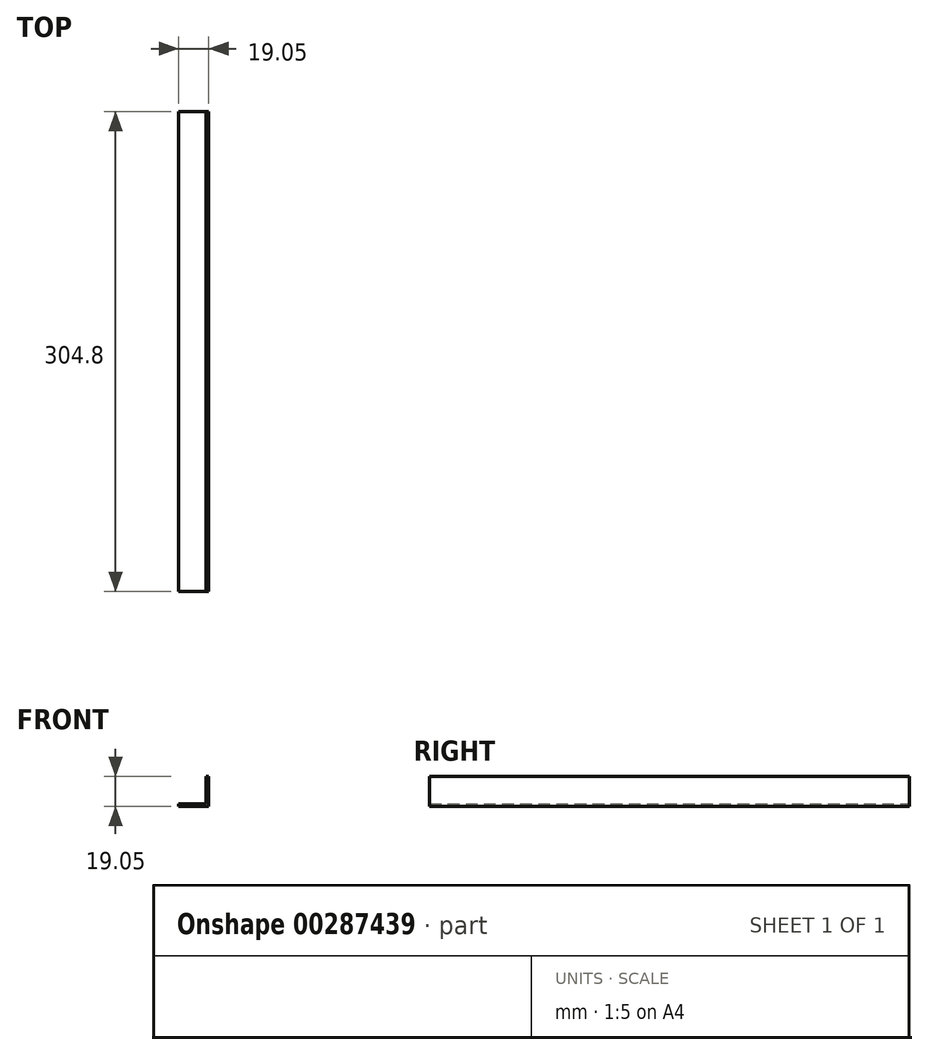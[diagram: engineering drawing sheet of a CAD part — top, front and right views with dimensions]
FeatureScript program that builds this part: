
annotation { "Feature Type Name" : "Feature", "Feature Type Description" : "" }
export const myFeature = defineFeature(function(context is Context, id is Id, definition is map)
    precondition{}
    {
        {
            var Q0;
            Q0=qCreatedBy(makeId("Front.planeOp"),FACE);
            var sketch = newSketch(context, id + "F0", { "sketchPlane" : qUnion([Q0])});
            skLineSegment(sketch, "E0", {"start": v(-19.05, 0) * mm, "end": v(0, 0) * mm});
            skLineSegment(sketch, "E1", {"start": v(0, 0) * mm, "end": v(0, 19.05) * mm});
            skLineSegment(sketch, "E2.0", {"start": v(-1.59, 1.59) * mm, "end": v(-1.59, 19.05) * mm});
            skLineSegment(sketch, "E2.1", {"start": v(-19.05, 1.59) * mm, "end": v(-1.59, 1.59) * mm});
            skLineSegment(sketch, "E3", {"start": v(0, 19.05) * mm, "end": v(-1.59, 19.05) * mm});
            skLineSegment(sketch, "E4", {"start": v(-19.05, 1.59) * mm, "end": v(-19.05, 0) * mm});
            skSolve(sketch);
        }
        {
            var Q0;
            Q0 = qSketchRegion(id + "F0", true);
            extrude(context, id + "F1", {"entities" : qUnion([Q0]), "depth" : 304.8 * mm});
        }
    });
